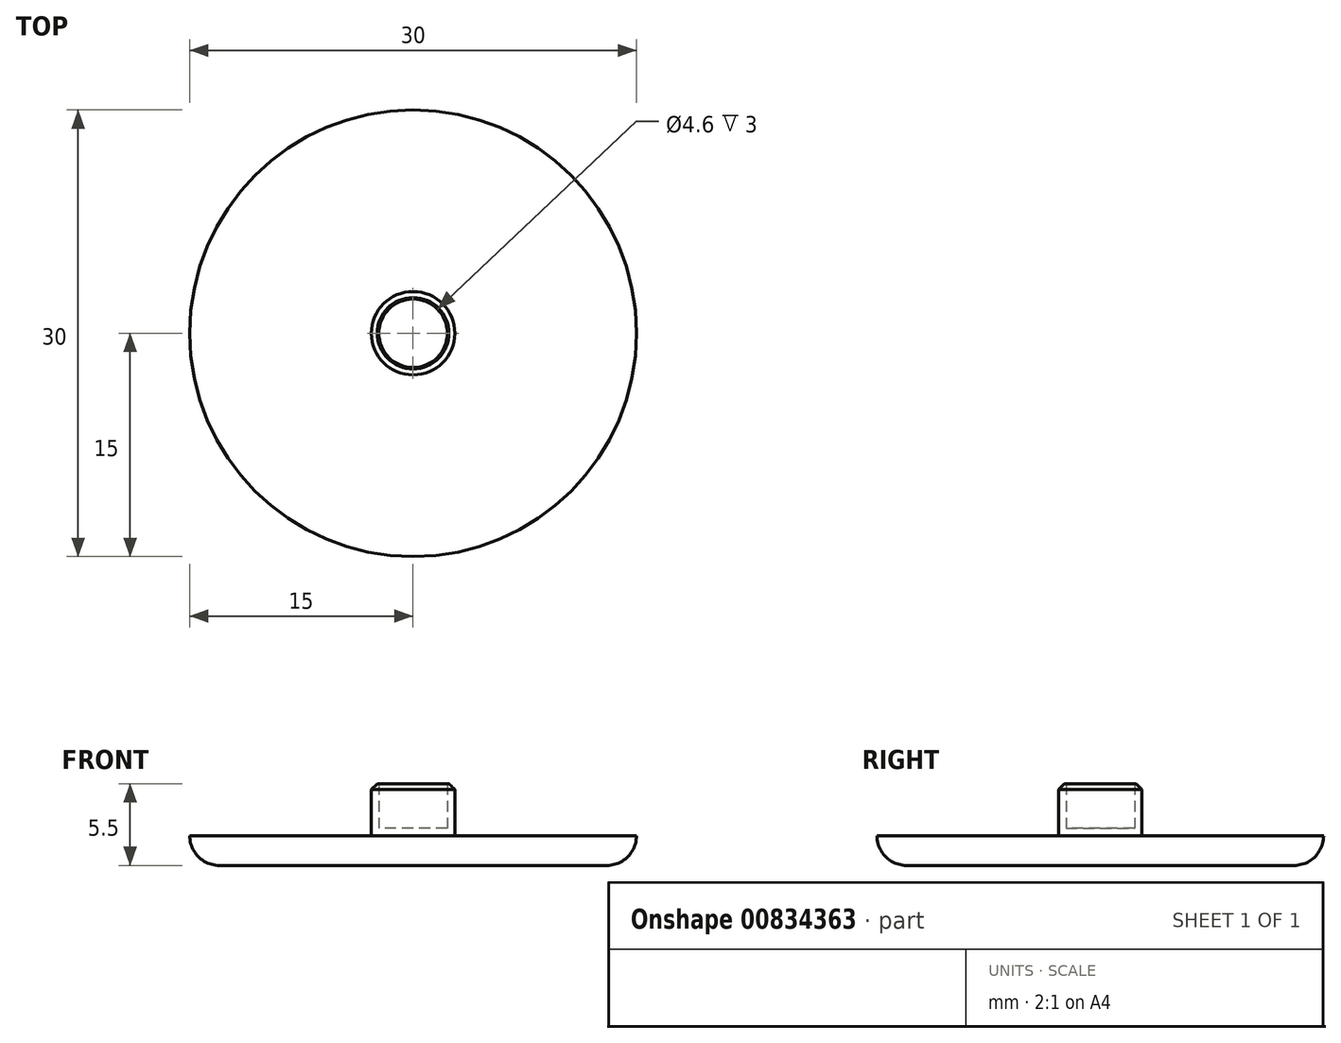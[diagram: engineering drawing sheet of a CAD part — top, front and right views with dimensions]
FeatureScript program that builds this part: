
annotation { "Feature Type Name" : "Feature", "Feature Type Description" : "" }
export const myFeature = defineFeature(function(context is Context, id is Id, definition is map)
    precondition{}
    {
        {
            var Q0;
            Q0=qCreatedBy(makeId("Top.planeOp"),FACE);
            var sketch = newSketch(context, id + "F0", { "sketchPlane" : qUnion([Q0])});
            skCircle(sketch, "E0", {"center": v(0, 0) * mm, "radius": 2.8 * mm});
            skCircle(sketch, "E1", {"center": v(0, 0) * mm, "radius": 15 * mm});
            skSolve(sketch);
        }
        {
            var Q0;
            Q0=makeQuery(id+"F0.imprint","IMPRINT",FACE,{"disambiguationData":[TD([[makeQuery(id+"F0.imprint","IMPRINT",EDGE,{"derivedFrom":sQuery(id+"F0.wireOp",EDGE,"E0")}),1.0]])]});
            extrude(context, id + "F1", {"entities" : qUnion([Q0]), "depth" : 3.5 * mm, "offsetDistance" : 25 * mm});
        }
        {
            var Q0;
            Q0=makeQuery(id+"F1.opExtrude","CAP_FACE",FACE,{"disambiguationData":[OSD([sQuery(id+"F0.wireOp",EDGE,"E0")])],"isStart":false});
            shell(context, id + "F2", {"entities" : qUnion([Q0]), "thickness" : 0.5 * mm});
        }
        {
            var Q0;
            Q0 = qSketchRegion(id + "F0", true);
            var Q1;
            Q1=makeQuery(id+"F1.opExtrude","CAP_FACE",FACE,{"disambiguationData":[OSD([sQuery(id+"F0.wireOp",EDGE,"E0")])],"isStart":true});
            extrude(context, id + "F3", {"entities" : qUnion([Q0, Q1]), "operationType" : NewBodyOperationType.ADD, "oppositeDirection" : true, "depth" : 2 * mm, "offsetDistance" : 25 * mm});
        }
        {
            var Q0;
            Q0=makeQuery(id+"F3.opExtrude","CAP_EDGE",EDGE,{"disambiguationData":[OSD([sQuery(id+"F0.wireOp",EDGE,"E1")])],"isStart":false});
            fillet(context, id + "F4", {"entities" : qUnion([Q0]), "radius" : 2 * mm, "tangentPropagation" : true, "allowEdgeOverflow" : false});
        }
        {
            var Q0;
            Q0=makeQuery(id+"F1.opExtrude","CAP_EDGE",EDGE,{"disambiguationData":[OSD([sQuery(id+"F0.wireOp",EDGE,"E0")])],"isStart":false});
            chamfer(context, id + "F5", {"entities" : qUnion([Q0]), "width" : 0.4 * mm, "tangentPropagation" : true});
        }
    });
